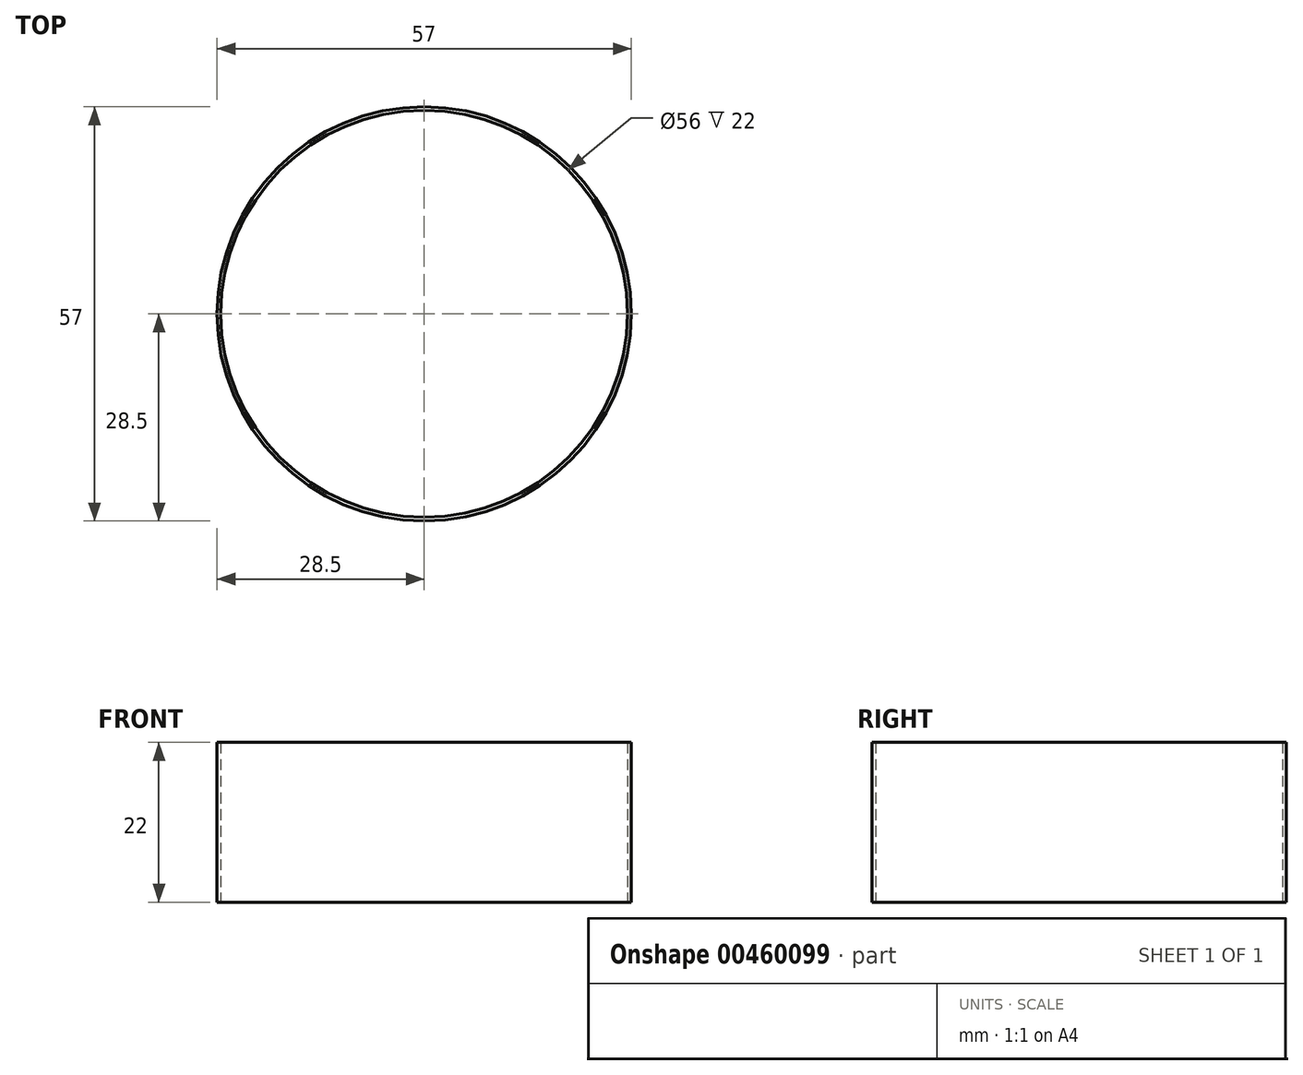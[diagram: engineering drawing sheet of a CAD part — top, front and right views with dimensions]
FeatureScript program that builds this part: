
annotation { "Feature Type Name" : "Feature", "Feature Type Description" : "" }
export const myFeature = defineFeature(function(context is Context, id is Id, definition is map)
    precondition{}
    {
        {
            var Q0;
            Q0=qCreatedBy(makeId("Top.planeOp"),FACE);
            var sketch = newSketch(context, id + "F0", { "sketchPlane" : qUnion([Q0])});
            skCircle(sketch, "E0", {"center": v(0, 0) * mm, "radius": 28.5 * mm});
            skLineSegment(sketch, "E1", {"start": v(0, 28.5) * mm, "end": v(0, -28.5) * mm});
            skLineSegment(sketch, "E2", {"start": v(-28.5, 0) * mm, "end": v(28.5, 0) * mm});
            skSolve(sketch);
        }
        {
            var Q0;
            Q0=makeQuery(id+"F0.imprint","IMPRINT",FACE,{"disambiguationData":[TD([[makeQuery(id+"F0.imprint","IMPRINT",EDGE,{"derivedFrom":sQuery(id+"F0.wireOp",EDGE,"E0")}),1.0]])]});
            extrude(context, id + "F1", {"entities" : qUnion([Q0]), "depth" : 22 * mm});
        }
        {
            var Q0;
            Q0=sQuery(id+"F0.wireOp",VERTEX,"E0.center");
            var Q1;
            Q1=makeQuery(id+"F1.opExtrude","SWEPT_BODY",BODY,{"disambiguationData":[OSD([sQuery(id+"F0.wireOp",EDGE,"E0")])]});
            hole(context, id + "F2", {"style" : HoleStyle.SIMPLE, "endStyle" : HoleEndStyle.THROUGH, "oppositeDirection" : true, "holeDiameter" : 56 * mm, "isTappedThrough" : true, "tappedDepth" : 12 * mm, "tapClearance" : 3, "startFromSketch" : true, "locations" : qUnion([Q0]), "scope" : qUnion([Q1])});
        }
    });
